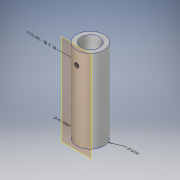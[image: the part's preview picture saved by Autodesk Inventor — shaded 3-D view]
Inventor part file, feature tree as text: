
AUTODESK INVENTOR PART (.ipt)
format: ipt  version: 2018.3 (Build 223284000, 284)  size: 130,048 bytes
history: native  units: in
note: dims shown in document units (in); Inventor stores cm internally (conversion verified against a paired STEP export)
features: hole x4, other x2, sketch x2, extrude x1, plane x1
ambient origin geometry x8: Origin, YZ Plane, XZ Plane, XY Plane, X Axis, Y Axis, Z Axis, Center Point
bodies: Solid1 (feature_tree)
feature tree (10):
  other  "Annotations"
  extrude  "Extrusion1"  Depth=1.0in
  hole  "Hole1"  [1 undecoded]
  plane  "Work Plane1"
  hole  "Hole2"  [1 undecoded]
  sketch  "Sketch1"  dims[d0=1.9in d1=0.0in d38=1.0in d39=1.0in]
  sketch  "Sketch2"  dims[d5=0.5in d6=0.119in d7=0.25in d8=0.5635in d9=1.9in d10=0.8108in d11=1.6in d12=0.104in d13=0.276in d14=0.375in d15=0.25in d16=0.5635in d17=0.4in d18=0.8108in d42=0.3in d23=0.0in d25=1.2359in d26=0.3358in d27=0.3804in d29=2.3209in d30=0.625in]
  hole  "Hole Note 1"  [1 undecoded]
  hole  "Hole Note 2"  [1 undecoded]
  other  "Diameter Dimension 1"
note: 4 required parameter values undecoded (feature->parameter linkage not recoverable at this tier; creation-order binding heuristic only, values carry confidence <= 0.55)
